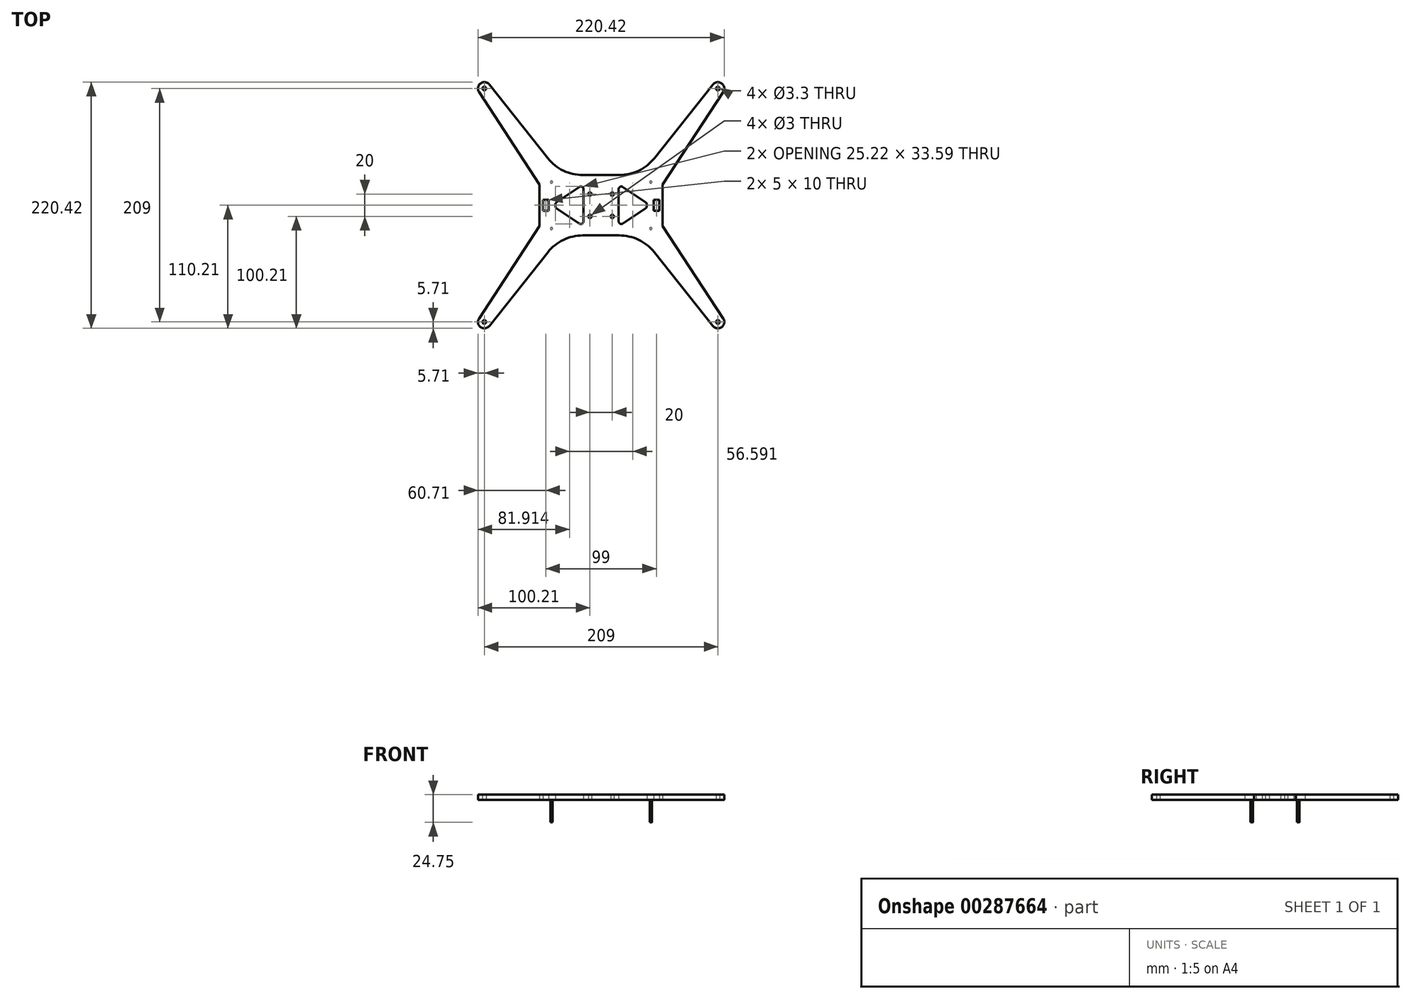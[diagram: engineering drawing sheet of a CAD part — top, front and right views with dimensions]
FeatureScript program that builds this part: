
annotation { "Feature Type Name" : "Feature", "Feature Type Description" : "" }
export const myFeature = defineFeature(function(context is Context, id is Id, definition is map)
    precondition{}
    {
        {
            var Q0;
            Q0=qCreatedBy(makeId("Top.planeOp"),FACE);
            var sketch = newSketch(context, id + "F0", { "sketchPlane" : qUnion([Q0])});
            skLineSegment(sketch, "E0", {"start": v(-39.8, -2.74) * mm, "end": v(-19.58, -16.37) * mm});
            skArc(sketch, "E1", {"start": v(-19.58, -16.37) * mm, "mid": v(-17.01, -16.5) * mm, "end": v(-15.68, -14.3) * mm});
            skLineSegment(sketch, "E2", {"start": v(-15.68, -14.3) * mm, "end": v(-15.68, 14.3) * mm});
            skArc(sketch, "E3", {"start": v(-15.68, 14.3) * mm, "mid": v(-17.01, 16.5) * mm, "end": v(-19.58, 16.37) * mm});
            skLineSegment(sketch, "E4", {"start": v(-19.58, 16.37) * mm, "end": v(-39.8, 2.74) * mm});
            skArc(sketch, "E5", {"start": v(-39.8, 2.74) * mm, "mid": v(-40.61, 1.84) * mm, "end": v(-40.9, 0.67) * mm});
            skLineSegment(sketch, "E6", {"start": v(-40.9, 0.67) * mm, "end": v(-40.9, -0.67) * mm});
            skArc(sketch, "E7", {"start": v(-40.9, -0.67) * mm, "mid": v(-40.61, -1.84) * mm, "end": v(-39.8, -2.74) * mm});
            skLineSegment(sketch, "E8", {"start": v(39.8, 2.74) * mm, "end": v(19.58, 16.37) * mm});
            skArc(sketch, "E9", {"start": v(19.58, 16.37) * mm, "mid": v(17.01, 16.5) * mm, "end": v(15.68, 14.3) * mm});
            skLineSegment(sketch, "E10", {"start": v(15.68, 14.3) * mm, "end": v(15.68, -14.3) * mm});
            skArc(sketch, "E11", {"start": v(15.68, -14.3) * mm, "mid": v(17.01, -16.5) * mm, "end": v(19.58, -16.37) * mm});
            skLineSegment(sketch, "E12", {"start": v(19.58, -16.37) * mm, "end": v(39.8, -2.74) * mm});
            skArc(sketch, "E13", {"start": v(39.8, -2.74) * mm, "mid": v(40.61, -1.84) * mm, "end": v(40.9, -0.67) * mm});
            skLineSegment(sketch, "E14", {"start": v(40.9, -0.67) * mm, "end": v(40.9, 0.67) * mm});
            skArc(sketch, "E15", {"start": v(40.9, 0.67) * mm, "mid": v(40.61, 1.84) * mm, "end": v(39.8, 2.74) * mm});
            skCircle(sketch, "E16", {"center": v(104.5, 104.5) * mm, "radius": 1.65 * mm});
            skCircle(sketch, "E17", {"center": v(44.44, 20.81) * mm, "radius": 3.56 * mm});
            skCircle(sketch, "E18", {"center": v(-104.5, 104.5) * mm, "radius": 1.65 * mm});
            skLineSegment(sketch, "E19", {"start": v(-100.03, 108.05) * mm, "end": v(-47.64, 42.12) * mm});
            skArc(sketch, "E20", {"start": v(-47.64, 42.12) * mm, "mid": v(-33.71, 30.98) * mm, "end": v(-16.32, 27) * mm});
            skLineSegment(sketch, "E21", {"start": v(-16.32, 27) * mm, "end": v(16.32, 27) * mm});
            skArc(sketch, "E22", {"start": v(16.32, 27) * mm, "mid": v(33.71, 30.98) * mm, "end": v(47.64, 42.12) * mm});
            skLineSegment(sketch, "E23", {"start": v(47.64, 42.12) * mm, "end": v(100.03, 108.05) * mm});
            skArc(sketch, "E24", {"start": v(100.03, 108.05) * mm, "mid": v(107.84, 109.12) * mm, "end": v(109.27, 101.37) * mm});
            skLineSegment(sketch, "E25", {"start": v(109.27, 101.37) * mm, "end": v(55, 18.66) * mm});
            skLineSegment(sketch, "E26", {"start": v(55, 18.66) * mm, "end": v(55, -18.66) * mm});
            skLineSegment(sketch, "E27", {"start": v(55, -18.66) * mm, "end": v(109.27, -101.37) * mm});
            skArc(sketch, "E28", {"start": v(109.27, -101.37) * mm, "mid": v(107.84, -109.12) * mm, "end": v(100.03, -108.05) * mm});
            skLineSegment(sketch, "E29", {"start": v(100.03, -108.05) * mm, "end": v(47.64, -42.12) * mm});
            skArc(sketch, "E30", {"start": v(47.64, -42.12) * mm, "mid": v(33.71, -30.98) * mm, "end": v(16.33, -27) * mm});
            skLineSegment(sketch, "E31", {"start": v(16.33, -27) * mm, "end": v(-16.33, -27) * mm});
            skArc(sketch, "E32", {"start": v(-16.33, -27) * mm, "mid": v(-33.71, -30.98) * mm, "end": v(-47.64, -42.12) * mm});
            skLineSegment(sketch, "E33", {"start": v(-47.64, -42.12) * mm, "end": v(-100.03, -108.05) * mm});
            skArc(sketch, "E34", {"start": v(-100.03, -108.05) * mm, "mid": v(-107.84, -109.12) * mm, "end": v(-109.27, -101.37) * mm});
            skLineSegment(sketch, "E35", {"start": v(-109.27, -101.37) * mm, "end": v(-55, -18.66) * mm});
            skLineSegment(sketch, "E36", {"start": v(-55, -18.66) * mm, "end": v(-55, 18.66) * mm});
            skLineSegment(sketch, "E37", {"start": v(-55, 18.66) * mm, "end": v(-109.27, 101.37) * mm});
            skArc(sketch, "E38", {"start": v(-109.27, 101.37) * mm, "mid": v(-107.84, 109.12) * mm, "end": v(-100.03, 108.05) * mm});
            skCircle(sketch, "E39", {"center": v(-44.44, 20.81) * mm, "radius": 3.56 * mm});
            skCircle(sketch, "E40", {"center": v(10, 10) * mm, "radius": 1.5 * mm});
            skCircle(sketch, "E41", {"center": v(-10, -10) * mm, "radius": 1.5 * mm});
            skCircle(sketch, "E42", {"center": v(10, -10) * mm, "radius": 1.5 * mm});
            skCircle(sketch, "E43", {"center": v(-10, 10) * mm, "radius": 1.5 * mm});
            skLineSegment(sketch, "E44", {"start": v(-52, -5) * mm, "end": v(-47, -5) * mm});
            skLineSegment(sketch, "E45", {"start": v(-47, -5) * mm, "end": v(-47, 5) * mm});
            skLineSegment(sketch, "E46", {"start": v(-47, 5) * mm, "end": v(-52, 5) * mm});
            skLineSegment(sketch, "E47", {"start": v(-52, 5) * mm, "end": v(-52, -5) * mm});
            skLineSegment(sketch, "E48", {"start": v(47, 5) * mm, "end": v(47, -5) * mm});
            skLineSegment(sketch, "E49", {"start": v(47, -5) * mm, "end": v(52, -5) * mm});
            skLineSegment(sketch, "E50", {"start": v(52, -5) * mm, "end": v(52, 5) * mm});
            skLineSegment(sketch, "E51", {"start": v(52, 5) * mm, "end": v(47, 5) * mm});
            skCircle(sketch, "E52", {"center": v(-44.44, -20.8) * mm, "radius": 2.55 * mm});
            skCircle(sketch, "E53", {"center": v(-104.5, -104.5) * mm, "radius": 1.65 * mm});
            skCircle(sketch, "E54", {"center": v(44.44, -20.8) * mm, "radius": 2.55 * mm});
            skCircle(sketch, "E55", {"center": v(104.5, -104.5) * mm, "radius": 1.65 * mm});
            skSolve(sketch);
        }
        {
            var Q0;
            Q0=makeQuery(id+"F0.imprint","IMPRINT",FACE,{"disambiguationData":[TD([[makeQuery(id+"F0.imprint","IMPRINT",EDGE,{"derivedFrom":sQuery(id+"F0.wireOp",EDGE,"E0")}),-1.0]])]});
            extrude(context, id + "F1", {"entities" : qUnion([Q0]), "depth" : 4.75 * mm, "offsetDistance" : 25 * mm});
        }
        {
            var Q0;
            Q0=qCreatedBy(makeId("Top.planeOp"),FACE);
            var sketch = newSketch(context, id + "F2", { "sketchPlane" : qUnion([Q0])});
            skCircle(sketch, "E56", {"center": v(-44.44, 20.81) * mm, "radius": 1 * mm});
            skCircle(sketch, "E57", {"center": v(44.44, 20.81) * mm, "radius": 1 * mm});
            skCircle(sketch, "E58", {"center": v(-44.44, -20.8) * mm, "radius": 1 * mm});
            skCircle(sketch, "E59", {"center": v(44.44, -20.8) * mm, "radius": 1 * mm});
            skSolve(sketch);
        }
        {
            var Q0;
            Q0 = qSketchRegion(id + "F2", true);
            extrude(context, id + "F3", {"entities" : qUnion([Q0]), "oppositeDirection" : true, "depth" : 20 * mm, "offsetDistance" : 25 * mm});
        }
        {
            var Q0;
            Q0=makeQuery(id+"F1.opExtrude","CAP_FACE",FACE,{"disambiguationData":[OSD([sQuery(id+"F0.wireOp",EDGE,"E0"),sQuery(id+"F0.wireOp",EDGE,"E1"),sQuery(id+"F0.wireOp",EDGE,"E2"),sQuery(id+"F0.wireOp",EDGE,"E3"),sQuery(id+"F0.wireOp",EDGE,"E4"),sQuery(id+"F0.wireOp",EDGE,"E5"),sQuery(id+"F0.wireOp",EDGE,"E6"),sQuery(id+"F0.wireOp",EDGE,"E7"),sQuery(id+"F0.wireOp",EDGE,"E8"),sQuery(id+"F0.wireOp",EDGE,"E9"),sQuery(id+"F0.wireOp",EDGE,"E10"),sQuery(id+"F0.wireOp",EDGE,"E11"),sQuery(id+"F0.wireOp",EDGE,"E12"),sQuery(id+"F0.wireOp",EDGE,"E13"),sQuery(id+"F0.wireOp",EDGE,"E14"),sQuery(id+"F0.wireOp",EDGE,"E15"),sQuery(id+"F0.wireOp",EDGE,"E16"),sQuery(id+"F0.wireOp",EDGE,"E17"),sQuery(id+"F0.wireOp",EDGE,"E18"),sQuery(id+"F0.wireOp",EDGE,"E19"),sQuery(id+"F0.wireOp",EDGE,"E20"),sQuery(id+"F0.wireOp",EDGE,"E21"),sQuery(id+"F0.wireOp",EDGE,"E22"),sQuery(id+"F0.wireOp",EDGE,"E23"),sQuery(id+"F0.wireOp",EDGE,"E24"),sQuery(id+"F0.wireOp",EDGE,"E25"),sQuery(id+"F0.wireOp",EDGE,"E26"),sQuery(id+"F0.wireOp",EDGE,"E27"),sQuery(id+"F0.wireOp",EDGE,"E28"),sQuery(id+"F0.wireOp",EDGE,"E29"),sQuery(id+"F0.wireOp",EDGE,"E30"),sQuery(id+"F0.wireOp",EDGE,"E31"),sQuery(id+"F0.wireOp",EDGE,"E32"),sQuery(id+"F0.wireOp",EDGE,"E33"),sQuery(id+"F0.wireOp",EDGE,"E34"),sQuery(id+"F0.wireOp",EDGE,"E35"),sQuery(id+"F0.wireOp",EDGE,"E36"),sQuery(id+"F0.wireOp",EDGE,"E37"),sQuery(id+"F0.wireOp",EDGE,"E38"),sQuery(id+"F0.wireOp",EDGE,"E39"),sQuery(id+"F0.wireOp",EDGE,"E40"),sQuery(id+"F0.wireOp",EDGE,"E41"),sQuery(id+"F0.wireOp",EDGE,"E42"),sQuery(id+"F0.wireOp",EDGE,"E43"),sQuery(id+"F0.wireOp",EDGE,"E44"),sQuery(id+"F0.wireOp",EDGE,"E45"),sQuery(id+"F0.wireOp",EDGE,"E46"),sQuery(id+"F0.wireOp",EDGE,"E47"),sQuery(id+"F0.wireOp",EDGE,"E48"),sQuery(id+"F0.wireOp",EDGE,"E49"),sQuery(id+"F0.wireOp",EDGE,"E50"),sQuery(id+"F0.wireOp",EDGE,"E51"),sQuery(id+"F0.wireOp",EDGE,"E52"),sQuery(id+"F0.wireOp",EDGE,"E53"),sQuery(id+"F0.wireOp",EDGE,"E54"),sQuery(id+"F0.wireOp",EDGE,"E55")])],"isStart":false});
            var sketch = newSketch(context, id + "F4", { "sketchPlane" : qUnion([Q0])});
            skCircle(sketch, "E60.0", {"center": v(-44.44, 20.81) * mm, "radius": 3.56 * mm});
            skCircle(sketch, "E61.0", {"center": v(-44.44, -20.8) * mm, "radius": 2.55 * mm});
            skCircle(sketch, "E62.0", {"center": v(44.44, 20.81) * mm, "radius": 3.56 * mm});
            skCircle(sketch, "E63.0", {"center": v(44.44, -20.8) * mm, "radius": 2.55 * mm});
            skSolve(sketch);
        }
        {
            var Q0;
            Q0 = qSketchRegion(id + "F4", true);
            extrude(context, id + "F5", {"entities" : qUnion([Q0]), "operationType" : NewBodyOperationType.ADD, "oppositeDirection" : true, "depth" : 4.75 * mm, "offsetDistance" : 25 * mm});
        }
    });
